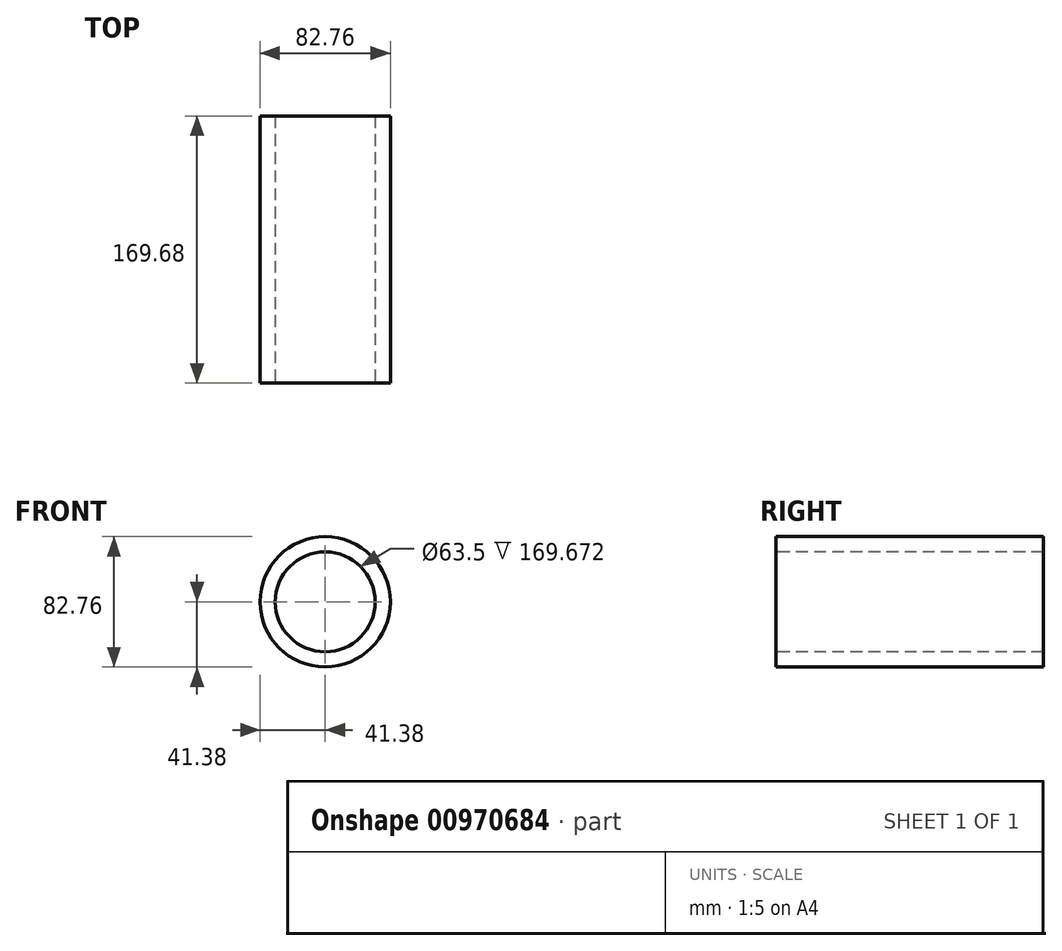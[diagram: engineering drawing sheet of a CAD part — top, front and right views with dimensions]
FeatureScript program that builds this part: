
annotation { "Feature Type Name" : "Feature", "Feature Type Description" : "" }
export const myFeature = defineFeature(function(context is Context, id is Id, definition is map)
    precondition{}
    {
        {
            var Q0;
            Q0=qCreatedBy(makeId("Front.planeOp"),FACE);
            var sketch = newSketch(context, id + "F0", { "sketchPlane" : qUnion([Q0])});
            skCircle(sketch, "E0", {"center": v(0, 0) * mm, "radius": 41.38 * mm});
            skSolve(sketch);
        }
        {
            var Q0;
            Q0=makeQuery(id+"F0.imprint","IMPRINT",FACE,{"disambiguationData":[TD([[makeQuery(id+"F0.imprint","IMPRINT",EDGE,{"derivedFrom":sQuery(id+"F0.wireOp",EDGE,"E0")}),1.0]])]});
            extrude(context, id + "F1", {"entities" : qUnion([Q0]), "endBound" : BoundingType.SYMMETRIC, "depth" : 169.67 * mm, "offsetDistance" : 25.4 * mm});
        }
        {
            var Q0;
            Q0=makeQuery(id+"F1.opExtrude","CAP_FACE",FACE,{"disambiguationData":[OSD([sQuery(id+"F0.wireOp",EDGE,"E0")])],"isStart":false});
            var sketch = newSketch(context, id + "F2", { "sketchPlane" : qUnion([Q0])});
            skPoint(sketch, "E1", {"position": v(0, 0) * mm});
            skSolve(sketch);
        }
        {
            var Q0;
            Q0=sQuery(id+"F2.wireOp",VERTEX,"E1");
            var Q1;
            Q1=makeQuery(id+"F1.opExtrude","SWEPT_BODY",BODY,{"disambiguationData":[OSD([sQuery(id+"F0.wireOp",EDGE,"E0")])]});
            hole(context, id + "F3", {"style" : HoleStyle.SIMPLE, "endStyle" : HoleEndStyle.THROUGH, "holeDiameter" : 63.5 * mm, "majorDiameter" : 6.35 * mm, "isTappedThrough" : true, "tappedDepth" : 12.7 * mm, "tapClearance" : 3, "locations" : qUnion([Q0]), "scope" : qUnion([Q1])});
        }
    });
